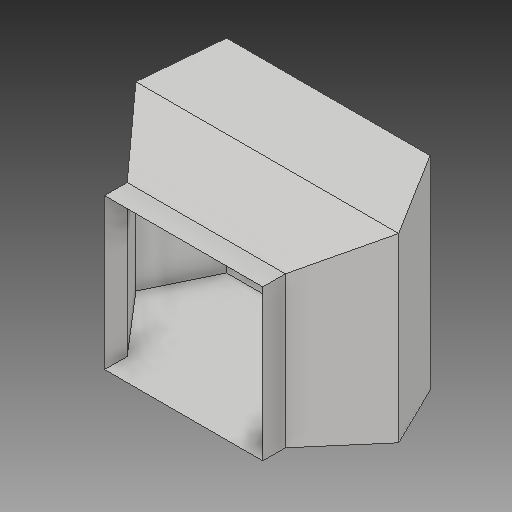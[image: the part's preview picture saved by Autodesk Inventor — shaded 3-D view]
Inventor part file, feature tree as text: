
AUTODESK INVENTOR PART (.ipt)
format: ipt  version: 2017 (Build 210142000, 142)  size: 183,808 bytes
history: native  units: in
note: dims shown in document units (in); Inventor stores cm internally (conversion verified against a paired STEP export)
features: sketch x4, other x2, loft x2, extrude x1, delete_face x1
ambient origin geometry x8: Origin, YZ Plane, XZ Plane, XY Plane, X Axis, Y Axis, Z Axis, Center Point
bodies: Solid1 (feature_tree)
feature tree (10):
  extrude  "connection"  Depth=2.7in
  sketch  "Sketch4"  dims[d281=6.6667in d283=5.8147in d284=8.02in d285=0.0in d286=90.0deg d287=0.0in d288=90.0deg d289=0.0in d290=90.0deg d291=0.0in d292=90.0deg]
  other  "front half of room"
  sketch  "Sketch2"  dims[d33=1.0in d221=9.0in]
  other  "front of room"
  sketch  "Sketch3"  dims[d222=9.0in d280=7.0in]
  loft  "shell make 1"
  loft  "shell make 2"
  delete_face  "Delete Face5"
  sketch  "Sketch1"  dims[d12=1.0in d13=0.0in d14=2.7in d17=2.7in d26=69.0in d27=59.0in]
